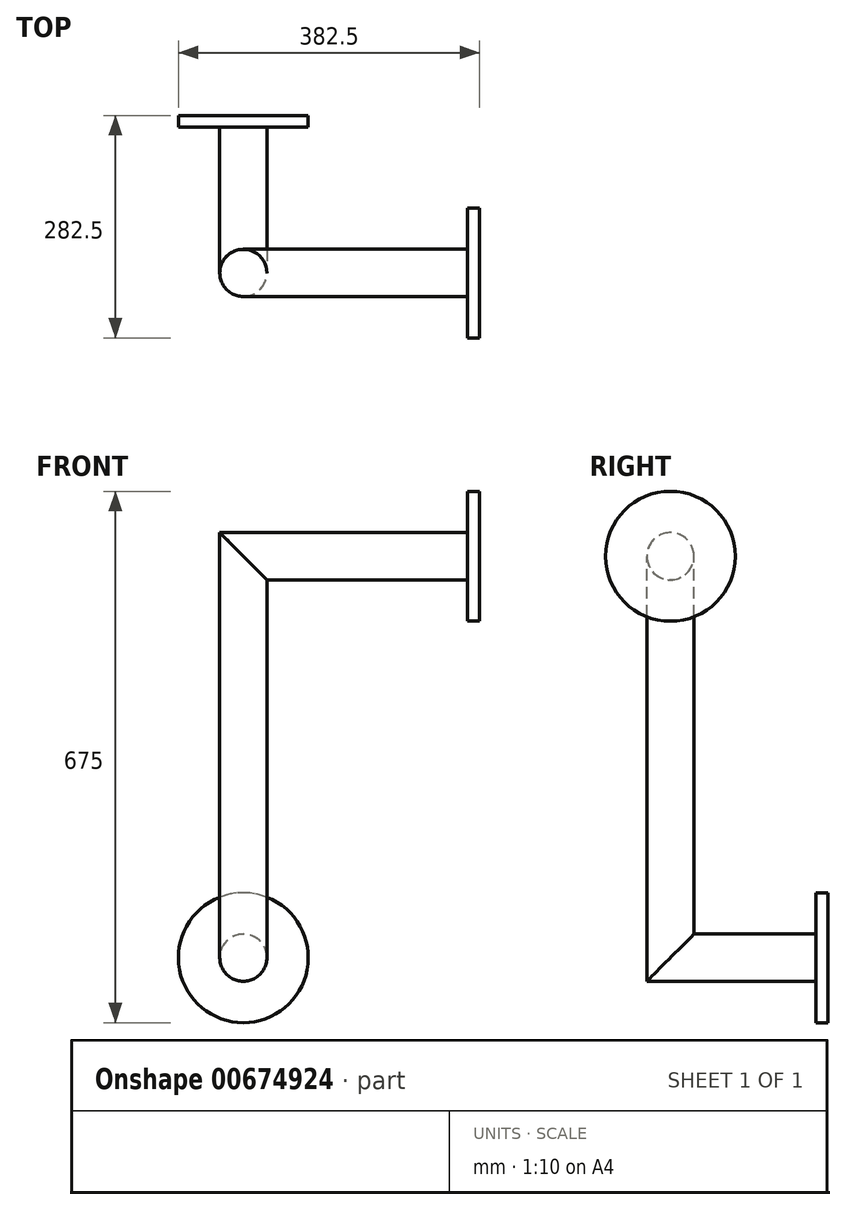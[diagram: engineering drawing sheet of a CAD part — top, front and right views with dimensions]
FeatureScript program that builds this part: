
annotation { "Feature Type Name" : "Feature", "Feature Type Description" : "" }
export const myFeature = defineFeature(function(context is Context, id is Id, definition is map)
    precondition{}
    {
        {
            var Q0;
            Q0=qCreatedBy(makeId("Front.planeOp"),FACE);
            var sketch = newSketch(context, id + "F0", { "sketchPlane" : qUnion([Q0])});
            skCircle(sketch, "E0", {"center": v(0, 0) * mm, "radius": 30 * mm});
            skCircle(sketch, "E1", {"center": v(0, 0) * mm, "radius": 82.5 * mm});
            skSolve(sketch);
        }
        {
            var Q0;
            Q0=qCreatedBy(makeId("Right.planeOp"),FACE);
            var sketch = newSketch(context, id + "F1", { "sketchPlane" : qUnion([Q0])});
            skLineSegment(sketch, "E2", {"start": v(0, 0) * mm, "end": v(-200, 0) * mm});
            skLineSegment(sketch, "E3", {"start": v(-200, 0) * mm, "end": v(-200, 510) * mm});
            skSolve(sketch);
        }
        {
            var Q0;
            Q0=qCreatedBy(makeId("Front.planeOp"),FACE);
            cPlane(context, id + "F2", {"entities" : qUnion([Q0]), "cplaneType" : CPlaneType.OFFSET, "offset" : 200 * mm, "width" : 150 * mm, "height" : 150 * mm});
        }
        {
            var Q0;
            Q0=qCreatedBy(id+"F2.planeOp",FACE);
            var sketch = newSketch(context, id + "F3", { "sketchPlane" : qUnion([Q0])});
            skPoint(sketch, "E4.0", {"position": v(0, 510) * mm});
            skLineSegment(sketch, "E5", {"start": v(0, 510) * mm, "end": v(300, 510) * mm});
            skSolve(sketch);
        }
        {
            var Q0;
            Q0=makeQuery(id+"F0.imprint","IMPRINT",FACE,{"disambiguationData":[TD([[makeQuery(id+"F0.imprint","IMPRINT",EDGE,{"derivedFrom":sQuery(id+"F0.wireOp",EDGE,"E0")}),1.0]])]});
            var Q1;
            Q1=sQuery(id+"F1.wireOp",EDGE,"E2");
            var Q2;
            Q2=sQuery(id+"F1.wireOp",EDGE,"E3");
            var Q3;
            Q3=sQuery(id+"F3.wireOp",EDGE,"E5");
            sweep(context, id + "F4", {"profiles" : qUnion([Q0]), "path" : qUnion([Q1, Q2, Q3])});
        }
        {
            var Q0;
            Q0=makeQuery(id+"F0.imprint","IMPRINT",FACE,{"disambiguationData":[TD([[makeQuery(id+"F0.imprint","IMPRINT",EDGE,{"derivedFrom":sQuery(id+"F0.wireOp",EDGE,"E0")}),-1.0]])]});
            extrude(context, id + "F5", {"entities" : qUnion([Q0]), "operationType" : NewBodyOperationType.ADD, "depth" : 15 * mm, "offsetDistance" : 25 * mm});
        }
        {
            var Q0;
            Q0=makeQuery(id+"F4.opSweep","CAP_FACE",FACE,{"disambiguationData":[OSD([sQuery(id+"F0.wireOp",EDGE,"E0"),sQuery(id+"F3.wireOp",VERTEX,"E5.end")])],"isStart":false});
            var sketch = newSketch(context, id + "F6", { "sketchPlane" : qUnion([Q0])});
            skCircle(sketch, "E6", {"center": v(-200, 510) * mm, "radius": 82.5 * mm});
            skSolve(sketch);
        }
        {
            var Q0;
            Q0=makeQuery(id+"F6.imprint","IMPRINT",FACE,{"disambiguationData":[TD([[makeQuery(id+"F6.imprint","IMPRINT",EDGE,{"derivedFrom":sQuery(id+"F6.wireOp",EDGE,"E6")}),1.0]])]});
            extrude(context, id + "F7", {"entities" : qUnion([Q0]), "operationType" : NewBodyOperationType.ADD, "oppositeDirection" : true, "depth" : 15 * mm, "offsetDistance" : 25 * mm});
        }
    });
